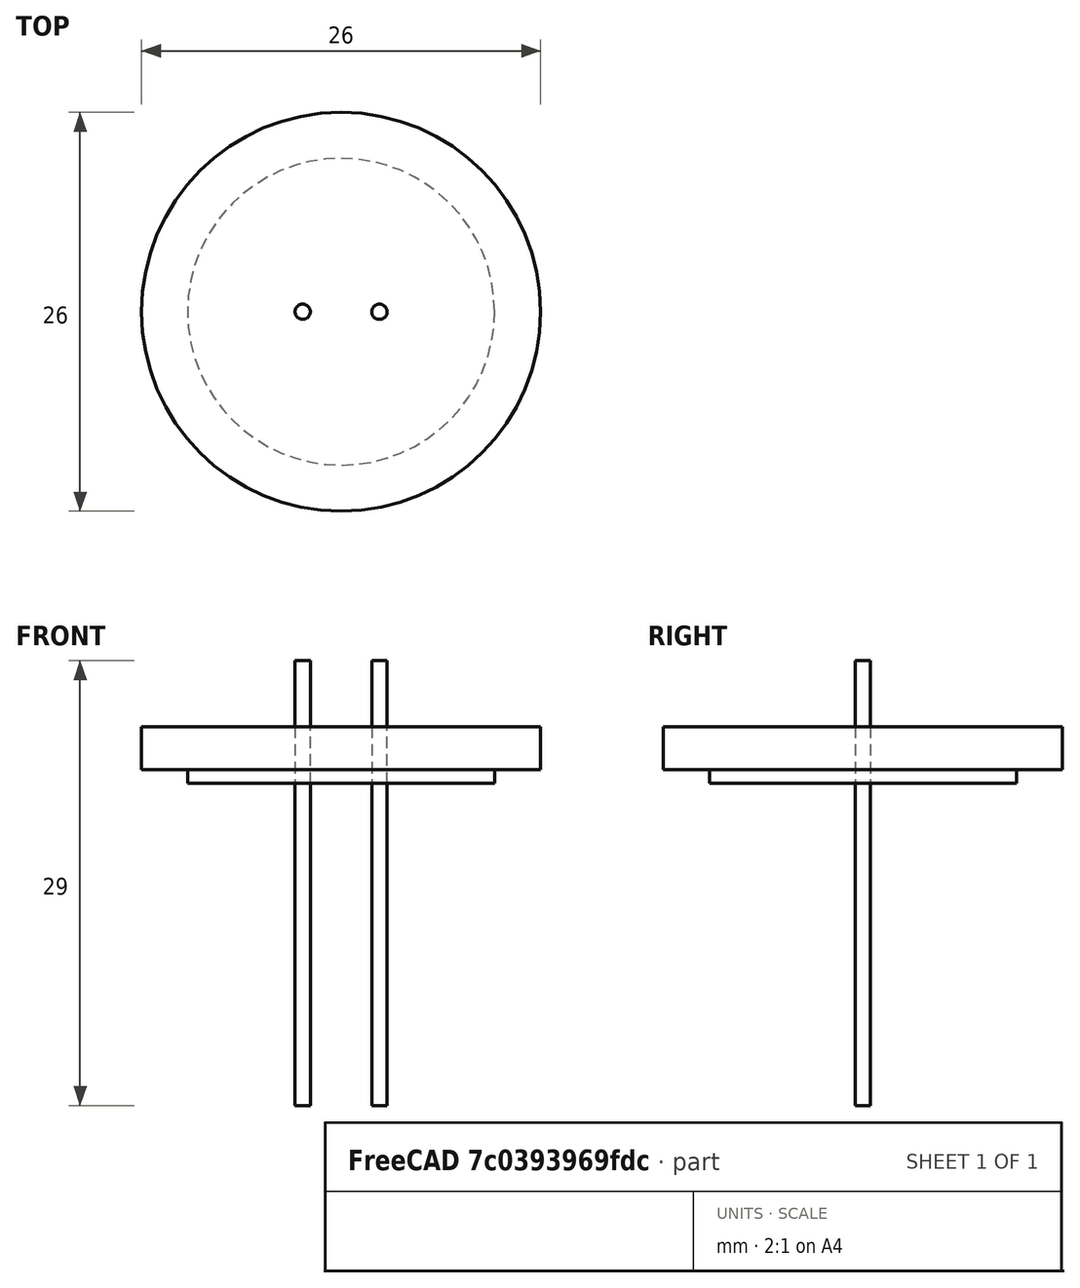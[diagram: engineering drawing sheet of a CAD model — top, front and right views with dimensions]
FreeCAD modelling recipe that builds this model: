
FCSTD DOCUMENT  (FreeCAD 0.21R0.21.2)
Label: TungstenFilamentBase
License: All rights reserved
LicenseURL: http://en.wikipedia.org/wiki/All_rights_reserved
objects: Part::Cylinder×6, Part::Compound×2, Part::MultiFuse×1, Part::Cut×1
note: 10 computed .brp shape members not serialized (recipe doc carries the construction recipe); baked Part::Feature solids carry a one-line shape summary decoded from their .brp

FEATURE [Part::Cylinder] Cylinder
  Angle = 360
  AttacherType = Attacher::AttachEngine3D
  FirstAngle = 0
  Height = 2.8
  Placement = pos=(0,0,0.9) rot=(0,0,1;0rad)
  Radius = 13
  SecondAngle = 0
FEATURE [Part::Cylinder] Cylinder001
  Angle = 360
  AttacherType = Attacher::AttachEngine3D
  FirstAngle = 0
  Height = 3.7
  Radius = 10
  SecondAngle = 0
FEATURE [Part::MultiFuse] Fusion  label="CeramicsTemplate"
  Shapes = -> [Cylinder,Cylinder001]
FEATURE [Part::Cylinder] Cylinder002
  Angle = 360
  AttacherType = Attacher::AttachEngine3D
  FirstAngle = 0
  Height = 29
  Placement = pos=(2.5,0,-21) rot=(0,0,1;0rad)
  Radius = 0.5
  SecondAngle = 0
FEATURE [Part::Cylinder] Cylinder003
  Angle = 360
  AttacherType = Attacher::AttachEngine3D
  FirstAngle = 0
  Height = 29
  Placement = pos=(-2.5,0,-21) rot=(0,0,1;0rad)
  Radius = 0.5
  SecondAngle = 0
FEATURE [Part::Compound] Compound  label="Posts"
  Links = -> [Cylinder002,Cylinder003]
FEATURE [Part::Cylinder] Cylinder004
  Angle = 360
  AttacherType = Attacher::AttachEngine3D
  FirstAngle = 0
  Height = 29
  Placement = pos=(2.5,0,-21) rot=(0,0,1;0rad)
  Radius = 0.5
  SecondAngle = 0
FEATURE [Part::Cylinder] Cylinder005
  Angle = 360
  AttacherType = Attacher::AttachEngine3D
  FirstAngle = 0
  Height = 29
  Placement = pos=(-2.5,0,-21) rot=(0,0,1;0rad)
  Radius = 0.5
  SecondAngle = 0
FEATURE [Part::Compound] Compound001  label="Posts001"
  Links = -> [Cylinder004,Cylinder005]
FEATURE [Part::Cut] Cut  label="CeramicsDisk"
  Base = -> Fusion
  Tool = -> Compound001
